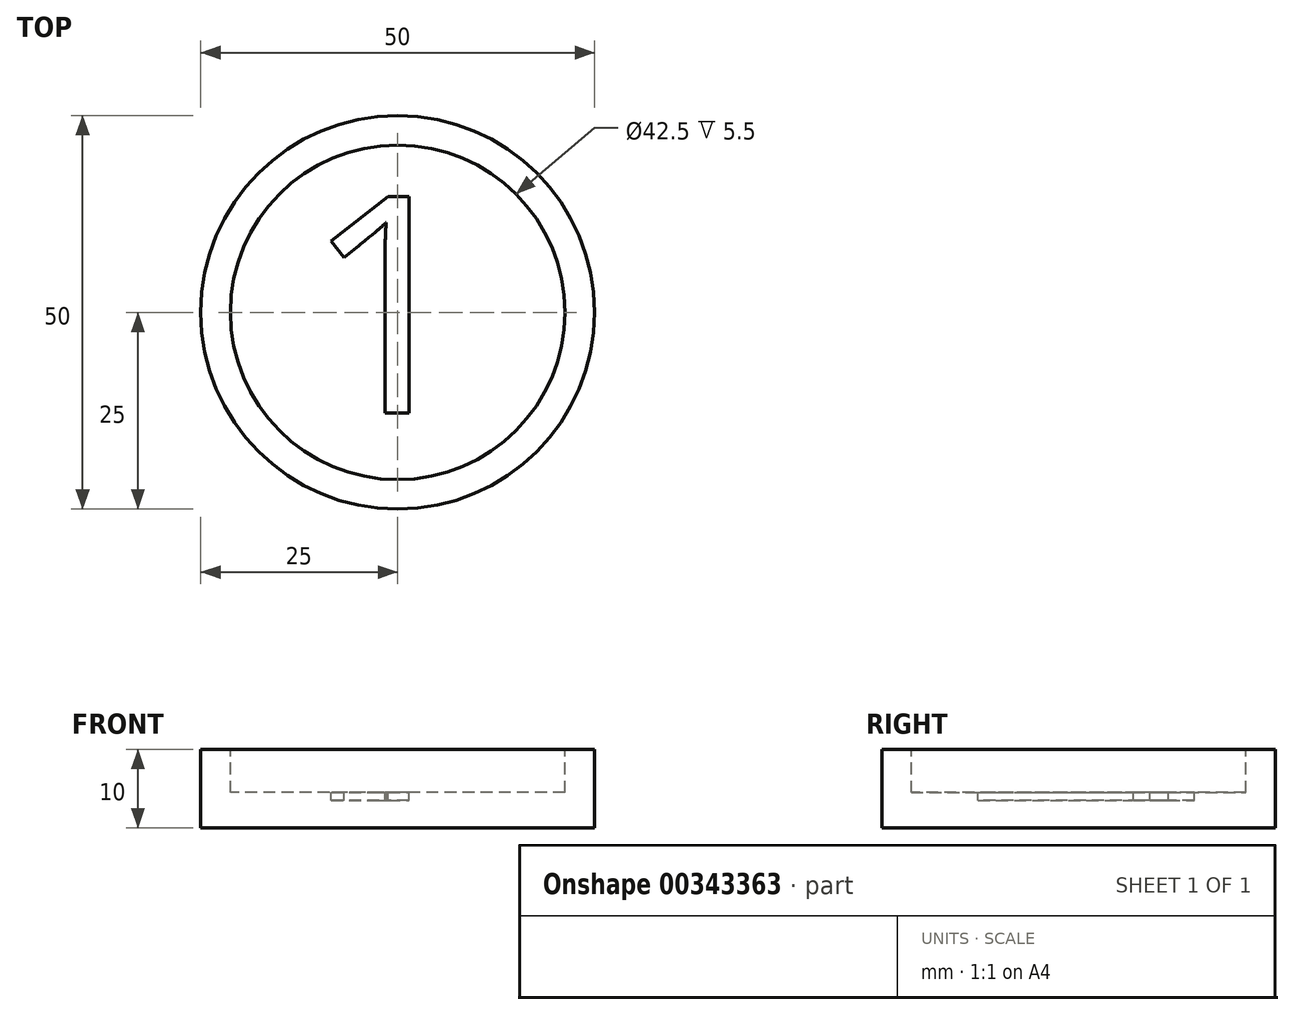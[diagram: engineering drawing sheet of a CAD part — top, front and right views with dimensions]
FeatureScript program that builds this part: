
annotation { "Feature Type Name" : "Feature", "Feature Type Description" : "" }
export const myFeature = defineFeature(function(context is Context, id is Id, definition is map)
    precondition{}
    {
        {
            var Q0;
            Q0=qCreatedBy(makeId("Top.planeOp"),FACE);
            var sketch = newSketch(context, id + "F0", { "sketchPlane" : qUnion([Q0])});
            skCircle(sketch, "E0", {"center": v(0, 0) * mm, "radius": 25 * mm});
            skSolve(sketch);
        }
        {
            var Q0;
            Q0 = qSketchRegion(id + "F0", true);
            extrude(context, id + "F1", {"entities" : qUnion([Q0]), "depth" : 10 * mm});
        }
        {
            var Q0;
            Q0=makeQuery(id+"F1.opExtrude","CAP_FACE",FACE,{"disambiguationData":[OSD([sQuery(id+"F0.wireOp",EDGE,"E0")])],"isStart":false});
            var sketch = newSketch(context, id + "F2", { "sketchPlane" : qUnion([Q0])});
            skCircle(sketch, "E1", {"center": v(0, 0) * mm, "radius": 21.25 * mm});
            skSolve(sketch);
        }
        {
            var Q0;
            Q0 = qSketchRegion(id + "F2", true);
            extrude(context, id + "F3", {"entities" : qUnion([Q0]), "operationType" : NewBodyOperationType.REMOVE, "oppositeDirection" : true, "depth" : 5.5 * mm});
        }
        {
            var Q0;
            Q0=makeQuery(id+"F3.boolean.opBoolean","COPY",FACE,{"derivedFrom":makeQuery(id+"F3.opExtrude","CAP_FACE",FACE,{"disambiguationData":[OSD([sQuery(id+"F2.wireOp",EDGE,"E1")])],"isStart":false})});
            var sketch = newSketch(context, id + "F4", { "sketchPlane" : qUnion([Q0])});
            skText(sketch, "E2", { "text": "1", "fontName": "OpenSans-Regular.ttf"});
            const initialGuessF4  = {"E2": [-0.012, -0.01278, 1, 0, 0.02772]};
            skSetInitialGuess(sketch, initialGuessF4);
            skSolve(sketch);
        }
        {
            var Q0;
            Q0 = qSketchRegion(id + "F4", true);
            extrude(context, id + "F5", {"entities" : qUnion([Q0]), "operationType" : NewBodyOperationType.REMOVE, "oppositeDirection" : true, "depth" : 1 * mm});
        }
    });
